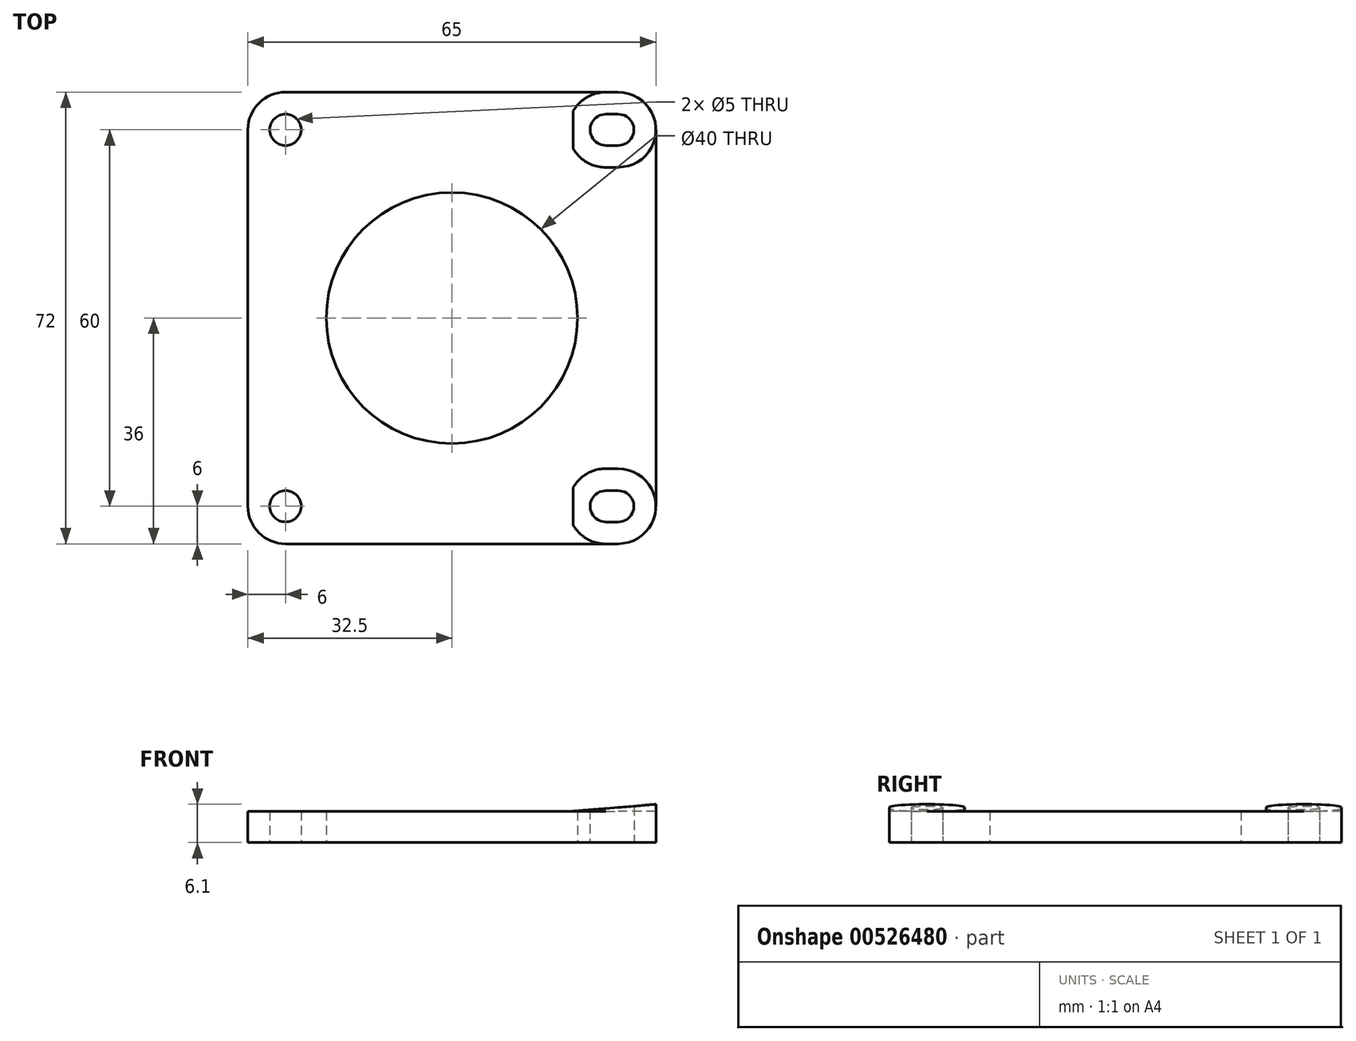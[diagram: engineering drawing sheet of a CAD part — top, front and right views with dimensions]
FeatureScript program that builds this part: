
annotation { "Feature Type Name" : "Feature", "Feature Type Description" : "" }
export const myFeature = defineFeature(function(context is Context, id is Id, definition is map)
    precondition{}
    {
        {
            var Q0;
            Q0=qCreatedBy(makeId("Top.planeOp"),FACE);
            var sketch = newSketch(context, id + "F0", { "sketchPlane" : qUnion([Q0])});
            skLineSegment(sketch, "E0.bottom", {"start": v(-32.5, -36) * mm, "end": v(32.5, -36) * mm});
            skLineSegment(sketch, "E0.top", {"start": v(-32.5, 36) * mm, "end": v(32.5, 36) * mm});
            skLineSegment(sketch, "E0.left", {"start": v(-32.5, -36) * mm, "end": v(-32.5, 36) * mm});
            skLineSegment(sketch, "E0.right", {"start": v(32.5, -36) * mm, "end": v(32.5, 36) * mm});
            skPoint(sketch, "E0.middle", {"position": v(0, 0) * mm});
            skCircle(sketch, "E1", {"center": v(0, 0) * mm, "radius": 20 * mm});
            skCircle(sketch, "E2", {"center": v(-26.5, 30) * mm, "radius": 2.5 * mm});
            skCircle(sketch, "E3", {"center": v(-26.5, -30) * mm, "radius": 2.5 * mm});
            skLineSegment(sketch, "E4", {"start": v(-26.5, -30) * mm, "end": v(-26.5, 30) * mm, "construction": true});
            skLineSegment(sketch, "E5", {"start": v(-26.5, 0) * mm, "end": v(0, 0) * mm, "construction": true});
            skLineSegment(sketch, "E6", {"start": v(24.5, -30) * mm, "end": v(26.5, -30) * mm, "construction": true});
            skLineSegment(sketch, "E7", {"start": v(24.5, 30) * mm, "end": v(26.5, 30) * mm, "construction": true});
            skArc(sketch, "E8.0.startCap", {"start": v(24.5, -32.5) * mm, "mid": v(22, -30) * mm, "end": v(24.5, -27.5) * mm});
            skArc(sketch, "E8.0.endCap", {"start": v(26.5, -27.5) * mm, "mid": v(29, -30) * mm, "end": v(26.5, -32.5) * mm});
            skLineSegment(sketch, "E8.0.left", {"start": v(24.5, -27.5) * mm, "end": v(26.5, -27.5) * mm});
            skLineSegment(sketch, "E8.0.right", {"start": v(24.5, -32.5) * mm, "end": v(26.5, -32.5) * mm});
            skArc(sketch, "E9.0.startCap", {"start": v(24.5, 27.5) * mm, "mid": v(22, 30) * mm, "end": v(24.5, 32.5) * mm});
            skArc(sketch, "E9.0.endCap", {"start": v(26.5, 32.5) * mm, "mid": v(29, 30) * mm, "end": v(26.5, 27.5) * mm});
            skLineSegment(sketch, "E9.0.left", {"start": v(24.5, 32.5) * mm, "end": v(26.5, 32.5) * mm});
            skLineSegment(sketch, "E9.0.right", {"start": v(24.5, 27.5) * mm, "end": v(26.5, 27.5) * mm});
            skSolve(sketch);
        }
        {
            var Q0;
            Q0 = qSketchRegion(id + "F0", true);
            extrude(context, id + "F1", {"entities" : qUnion([Q0]), "depth" : 5 * mm, "offsetDistance" : 25 * mm});
        }
        {
            var Q0;
            Q0=makeQuery(id+"F1.opExtrude","CAP_FACE",FACE,{"disambiguationData":[OSD([sQuery(id+"F0.wireOp",EDGE,"E0.bottom"),sQuery(id+"F0.wireOp",EDGE,"E0.top"),sQuery(id+"F0.wireOp",EDGE,"E0.left"),sQuery(id+"F0.wireOp",EDGE,"E0.right"),sQuery(id+"F0.wireOp",EDGE,"E1"),sQuery(id+"F0.wireOp",EDGE,"E2"),sQuery(id+"F0.wireOp",EDGE,"E3"),sQuery(id+"F0.wireOp",EDGE,"E8.0.startCap"),sQuery(id+"F0.wireOp",EDGE,"E8.0.endCap"),sQuery(id+"F0.wireOp",EDGE,"E8.0.left"),sQuery(id+"F0.wireOp",EDGE,"E8.0.right"),sQuery(id+"F0.wireOp",EDGE,"E9.0.startCap"),sQuery(id+"F0.wireOp",EDGE,"E9.0.endCap"),sQuery(id+"F0.wireOp",EDGE,"E9.0.left"),sQuery(id+"F0.wireOp",EDGE,"E9.0.right")])],"isStart":false});
            var sketch = newSketch(context, id + "F2", { "sketchPlane" : qUnion([Q0])});
            skLineSegment(sketch, "E10.0", {"start": v(24.5, -24) * mm, "end": v(26.5, -24) * mm});
            skArc(sketch, "E10.1", {"start": v(24.5, -36) * mm, "mid": v(18.5, -30) * mm, "end": v(24.5, -24) * mm});
            skLineSegment(sketch, "E10.2", {"start": v(24.5, -36) * mm, "end": v(26.5, -36) * mm});
            skArc(sketch, "E10.3", {"start": v(26.5, -24) * mm, "mid": v(32.5, -30) * mm, "end": v(26.5, -36) * mm});
            skLineSegment(sketch, "E11.0", {"start": v(24.5, 24) * mm, "end": v(26.5, 24) * mm});
            skArc(sketch, "E11.1", {"start": v(24.5, 24) * mm, "mid": v(18.5, 30) * mm, "end": v(24.5, 36) * mm});
            skLineSegment(sketch, "E11.2", {"start": v(24.5, 36) * mm, "end": v(26.5, 36) * mm});
            skArc(sketch, "E11.3", {"start": v(26.5, 36) * mm, "mid": v(32.5, 30) * mm, "end": v(26.5, 24) * mm});
            skSolve(sketch);
        }
        {
            var Q0;
            {var subQ1=sQuery(id+"F2.wireOp",EDGE,"E10.0");Q0=makeQuery(id+"F2.imprint","IMPRINT",FACE,{"disambiguationData":[TD([[makeQuery(id+"F2.imprint","IMPRINT",EDGE,{"derivedFrom":subQ1}),-1.0]])]});}
            var Q1;
            {var subQ3=sQuery(id+"F2.wireOp",EDGE,"E11.0");Q1=makeQuery(id+"F2.imprint","IMPRINT",FACE,{"disambiguationData":[TD([[makeQuery(id+"F2.imprint","IMPRINT",EDGE,{"derivedFrom":subQ3}),1.0]])]});}
            extrude(context, id + "F3", {"entities" : qUnion([Q0, Q1]), "operationType" : NewBodyOperationType.ADD, "depth" : 1.1 * mm, "offsetDistance" : 25 * mm});
        }
        {
            var Q0;
            Q0=makeQuery(id+"F3.boolean.opBoolean","MERGE",FACE,{"derivedFrom":[makeQuery(id+"F1.opExtrude","SWEPT_FACE",FACE,{"disambiguationData":[OSD([sQuery(id+"F0.wireOp",EDGE,"E0.bottom")])]}),makeQuery(id+"F3.opExtrude","SWEPT_FACE",FACE,{"disambiguationData":[OSD([sQuery(id+"F2.wireOp",EDGE,"E10.2")])]})]});
            var sketch = newSketch(context, id + "F4", { "sketchPlane" : qUnion([Q0])});
            skLineSegment(sketch, "E12", {"start": v(32.5, 6.1) * mm, "end": v(19.3, 5) * mm});
            skLineSegment(sketch, "E13", {"start": v(18.5, 6.1) * mm, "end": v(32.5, 6.1) * mm});
            skLineSegment(sketch, "E14", {"start": v(18.5, 6.1) * mm, "end": v(18.5, 5) * mm});
            skLineSegment(sketch, "E15", {"start": v(18.5, 5) * mm, "end": v(19.3, 5) * mm});
            skSolve(sketch);
        }
        {
            var Q0;
            Q0 = qSketchRegion(id + "F4", true);
            extrude(context, id + "F5", {"entities" : qUnion([Q0]), "operationType" : NewBodyOperationType.REMOVE, "endBound" : BoundingType.THROUGH_ALL, "oppositeDirection" : true, "depth" : 25 * mm, "offsetDistance" : 25 * mm});
        }
        {
            var Q0;
            Q0=makeQuery(id+"F1.opExtrude","SWEPT_EDGE",EDGE,{"disambiguationData":[OSD([sQuery(id+"F0.wireOp",EDGE,"E0.bottom"),sQuery(id+"F0.wireOp",EDGE,"E0.left")])]});
            var Q1;
            Q1=makeQuery(id+"F1.opExtrude","SWEPT_EDGE",EDGE,{"disambiguationData":[OSD([sQuery(id+"F0.wireOp",EDGE,"E0.top"),sQuery(id+"F0.wireOp",EDGE,"E0.left")])]});
            var Q2;
            Q2=makeQuery(id+"F1.opExtrude","SWEPT_EDGE",EDGE,{"disambiguationData":[OSD([sQuery(id+"F0.wireOp",EDGE,"E0.top"),sQuery(id+"F0.wireOp",EDGE,"E0.right")])]});
            var Q3;
            Q3=makeQuery(id+"F1.opExtrude","SWEPT_EDGE",EDGE,{"disambiguationData":[OSD([sQuery(id+"F0.wireOp",EDGE,"E0.bottom"),sQuery(id+"F0.wireOp",EDGE,"E0.right")])]});
            fillet(context, id + "F6", {"entities" : qUnion([Q0, Q1, Q2, Q3]), "radius" : 6 * mm, "tangentPropagation" : true, "allowEdgeOverflow" : false});
        }
    });
